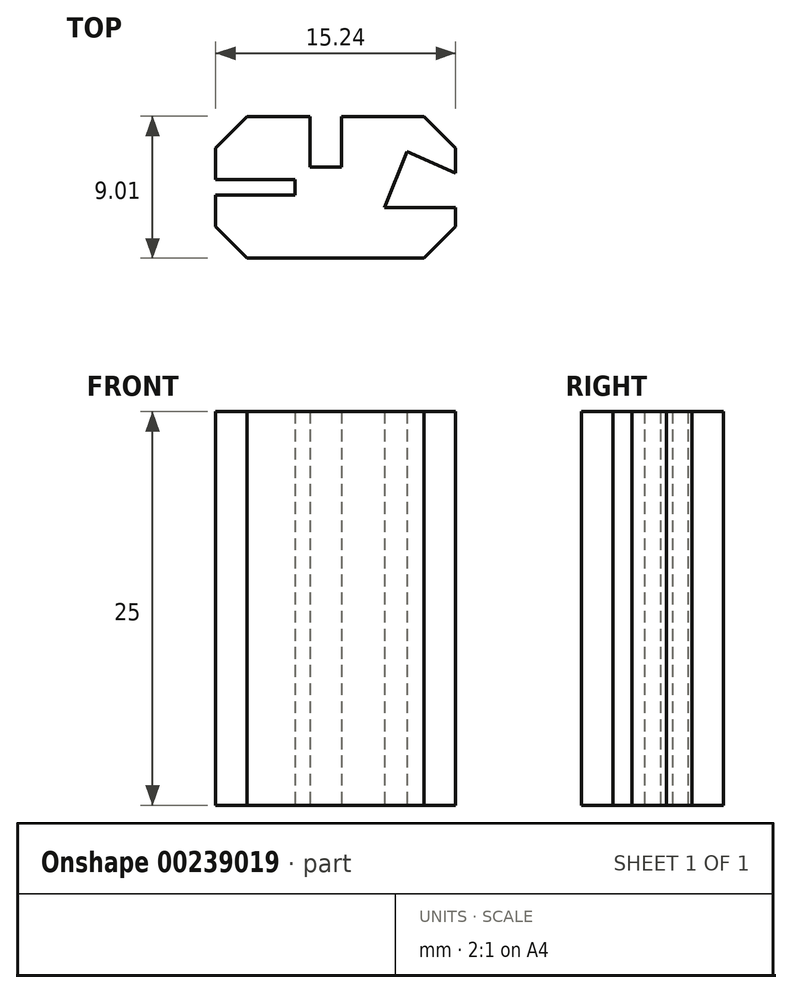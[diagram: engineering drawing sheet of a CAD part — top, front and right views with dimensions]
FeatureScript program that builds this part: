
annotation { "Feature Type Name" : "Feature", "Feature Type Description" : "" }
export const myFeature = defineFeature(function(context is Context, id is Id, definition is map)
    precondition{}
    {
        {
            var Q0;
            Q0=qCreatedBy(makeId("Top.planeOp"),FACE);
            var sketch = newSketch(context, id + "F0", { "sketchPlane" : qUnion([Q0])});
            skLineSegment(sketch, "E0", {"start": v(-15.26, -45.8) * mm, "end": v(-4.02, -45.8) * mm});
            skLineSegment(sketch, "E1", {"start": v(-4.02, -45.8) * mm, "end": v(-2.02, -43.8) * mm});
            skLineSegment(sketch, "E2", {"start": v(-15.26, -45.8) * mm, "end": v(-17.26, -43.8) * mm});
            skLineSegment(sketch, "E3", {"start": v(-17.26, -43.8) * mm, "end": v(-17.26, -41.8) * mm});
            skLineSegment(sketch, "E4", {"start": v(-17.26, -41.8) * mm, "end": v(-12.2, -41.8) * mm});
            skLineSegment(sketch, "E5", {"start": v(-12.2, -41.8) * mm, "end": v(-12.2, -40.8) * mm});
            skLineSegment(sketch, "E6", {"start": v(-12.2, -40.8) * mm, "end": v(-17.26, -40.8) * mm});
            skLineSegment(sketch, "E7", {"start": v(-17.26, -40.8) * mm, "end": v(-17.26, -38.8) * mm});
            skLineSegment(sketch, "E8", {"start": v(-17.26, -38.8) * mm, "end": v(-15.26, -36.8) * mm});
            skLineSegment(sketch, "E9", {"start": v(-15.26, -36.8) * mm, "end": v(-11.26, -36.8) * mm});
            skLineSegment(sketch, "E10", {"start": v(-11.26, -36.8) * mm, "end": v(-11.26, -40.02) * mm});
            skLineSegment(sketch, "E11", {"start": v(-11.26, -40.02) * mm, "end": v(-9.26, -40.02) * mm});
            skLineSegment(sketch, "E12", {"start": v(-9.26, -40.02) * mm, "end": v(-9.26, -36.8) * mm});
            skLineSegment(sketch, "E13", {"start": v(-9.26, -36.8) * mm, "end": v(-4.02, -36.8) * mm});
            skLineSegment(sketch, "E14", {"start": v(-4.02, -36.8) * mm, "end": v(-2.03, -38.8) * mm});
            skPoint(sketch, "E15.end.orphan", {"position": v(0, -36.92) * mm});
            skLineSegment(sketch, "E16", {"start": v(-2.03, -38.8) * mm, "end": v(-2.03, -40.4) * mm});
            skLineSegment(sketch, "E17", {"start": v(-2.02, -42.6) * mm, "end": v(-2.02, -43.8) * mm});
            skLineSegment(sketch, "E18", {"start": v(-2.02, -42.6) * mm, "end": v(-6.55, -42.6) * mm});
            skLineSegment(sketch, "E19", {"start": v(-6.55, -42.6) * mm, "end": v(-5.1, -39.03) * mm});
            skLineSegment(sketch, "E20", {"start": v(-2.03, -40.4) * mm, "end": v(-5.1, -39.03) * mm});
            skSolve(sketch);
        }
        {
            var Q0;
            Q0=makeQuery(id+"F0.imprint","IMPRINT",FACE,{"disambiguationData":[TD([[makeQuery(id+"F0.imprint","IMPRINT",EDGE,{"derivedFrom":sQuery(id+"F0.wireOp",EDGE,"E0")}),1.0]])]});
            extrude(context, id + "F1", {"entities" : qUnion([Q0]), "depth" : 25 * mm});
        }
    });
